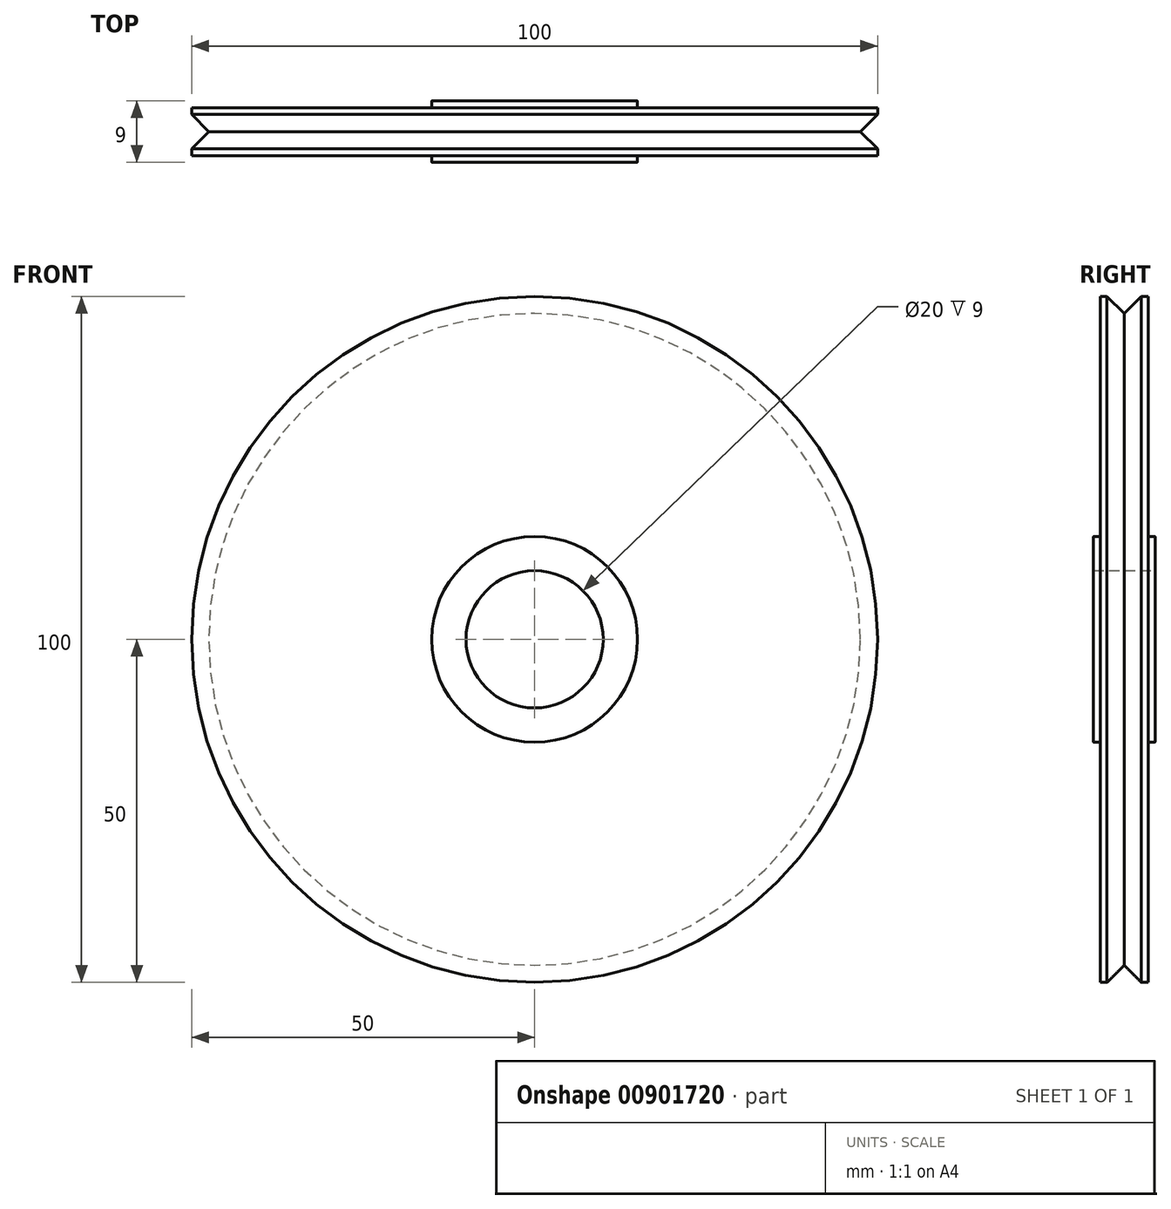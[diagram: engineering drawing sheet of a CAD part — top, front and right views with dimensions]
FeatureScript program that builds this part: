
annotation { "Feature Type Name" : "Feature", "Feature Type Description" : "" }
export const myFeature = defineFeature(function(context is Context, id is Id, definition is map)
    precondition{}
    {
        {
            var Q0;
            Q0=qCreatedBy(makeId("Front.planeOp"),FACE);
            var sketch = newSketch(context, id + "F0", { "sketchPlane" : qUnion([Q0])});
            skCircle(sketch, "E0", {"center": v(0, 0) * mm, "radius": 50 * mm});
            skSolve(sketch);
        }
        {
            var Q0;
            Q0=makeQuery(id+"F0.imprint","IMPRINT",FACE,{"disambiguationData":[TD([[makeQuery(id+"F0.imprint","IMPRINT",EDGE,{"derivedFrom":sQuery(id+"F0.wireOp",EDGE,"E0")}),1.0]])]});
            extrude(context, id + "F1", {"entities" : qUnion([Q0]), "depth" : 3.5 * mm, "offsetDistance" : 25 * mm});
        }
        {
            var Q0;
            Q0=makeQuery(id+"F1.opExtrude","CAP_FACE",FACE,{"disambiguationData":[OSD([sQuery(id+"F0.wireOp",EDGE,"E0")])],"isStart":false});
            chamfer(context, id + "F2", {"entities" : qUnion([Q0]), "width" : 2.5 * mm, "tangentPropagation" : true});
        }
        {
            var Q0;
            Q0=makeQuery(id+"F1.opExtrude","CAP_FACE",FACE,{"disambiguationData":[OSD([sQuery(id+"F0.wireOp",EDGE,"E0")])],"isStart":true});
            var sketch = newSketch(context, id + "F3", { "sketchPlane" : qUnion([Q0])});
            skCircle(sketch, "E1", {"center": v(0, 0) * mm, "radius": 10 * mm});
            skSolve(sketch);
        }
        {
            var Q0;
            Q0=makeQuery(id+"F3.imprint","IMPRINT",FACE,{"disambiguationData":[TD([[makeQuery(id+"F3.imprint","IMPRINT",EDGE,{"derivedFrom":sQuery(id+"F3.wireOp",EDGE,"E1")}),1.0]])]});
            extrude(context, id + "F4", {"entities" : qUnion([Q0]), "operationType" : NewBodyOperationType.REMOVE, "oppositeDirection" : true, "depth" : 3.5 * mm, "offsetDistance" : 25 * mm});
        }
        {
            var Q0;
            Q0=makeQuery(id+"F1.opExtrude","SWEPT_BODY",BODY,{"disambiguationData":[OSD([sQuery(id+"F0.wireOp",EDGE,"E0")])]});
            var Q1;
            Q1=makeQuery(id+"F1.opExtrude","CAP_FACE",FACE,{"disambiguationData":[OSD([sQuery(id+"F0.wireOp",EDGE,"E0")])],"isStart":false});
            mirror(context, id + "F5", {"operationType" : NewBodyOperationType.ADD, "entities" : qUnion([Q0]), "mirrorPlane" : qUnion([Q1])});
        }
        {
            var Q0;
            Q0=makeQuery(id+"F5.opPattern","COPY",FACE,{"derivedFrom":makeQuery(id+"F1.opExtrude","CAP_FACE",FACE,{"disambiguationData":[OSD([sQuery(id+"F0.wireOp",EDGE,"E0")])],"isStart":true}),"instanceName":"1"});
            var sketch = newSketch(context, id + "F6", { "sketchPlane" : qUnion([Q0])});
            skCircle(sketch, "E2", {"center": v(0, 0) * mm, "radius": 15 * mm});
            skSolve(sketch);
        }
        {
            var Q0;
            Q0=makeQuery(id+"F6.imprint","IMPRINT",FACE,{"disambiguationData":[TD([[makeQuery(id+"F6.imprint","IMPRINT",EDGE,{"derivedFrom":sQuery(id+"F6.wireOp",EDGE,"E2")}),1.0]])]});
            extrude(context, id + "F7", {"entities" : qUnion([Q0]), "operationType" : NewBodyOperationType.ADD, "depth" : 1 * mm, "offsetDistance" : 25 * mm});
        }
        {
            var Q0;
            Q0=makeQuery(id+"F1.opExtrude","CAP_FACE",FACE,{"disambiguationData":[OSD([sQuery(id+"F0.wireOp",EDGE,"E0")])],"isStart":true});
            var sketch = newSketch(context, id + "F8", { "sketchPlane" : qUnion([Q0])});
            skCircle(sketch, "E3", {"center": v(0, 0) * mm, "radius": 15 * mm});
            skSolve(sketch);
        }
        {
            var Q0;
            Q0=makeQuery(id+"F8.imprint","IMPRINT",FACE,{"disambiguationData":[TD([[makeQuery(id+"F8.imprint","IMPRINT",EDGE,{"derivedFrom":sQuery(id+"F8.wireOp",EDGE,"E3")}),1.0]])]});
            extrude(context, id + "F9", {"entities" : qUnion([Q0]), "operationType" : NewBodyOperationType.ADD, "depth" : 1 * mm, "offsetDistance" : 25 * mm});
        }
        {
            var Q0;
            Q0=makeQuery(id+"F7.opExtrude","CAP_EDGE",EDGE,{"disambiguationData":[OSD([sQuery(id+"F6.wireOp",EDGE,"E2")])],"isStart":false});
            var Q1;
            Q1=makeQuery(id+"F9.opExtrude","CAP_EDGE",EDGE,{"disambiguationData":[OSD([sQuery(id+"F8.wireOp",EDGE,"E3")])],"isStart":false});
            fillet(context, id + "F10", {"entities" : qUnion([Q0, Q1]), "radius" : 0.1 * mm, "tangentPropagation" : true, "allowEdgeOverflow" : false});
        }
    });
